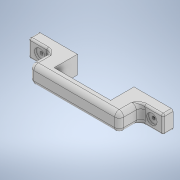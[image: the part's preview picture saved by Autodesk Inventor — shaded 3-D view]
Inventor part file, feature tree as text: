
AUTODESK INVENTOR PART (.ipt)
format: ipt  version: 2020 (Build 240168000, 168)  size: 222,208 bytes
history: native  units: mm
features: extrude x3, fillet x3, sketch x2, mirror x1, projected_geometry x1
ambient origin geometry x8: Origin, YZ Plane, XZ Plane, XY Plane, X Axis, Y Axis, Z Axis, Center Point
bodies: Solid1 (feature_tree)
feature tree (10):
  extrude  "Extrusion1"  Depth=50.0mm
  sketch  "Sketch2"  dims[d2=35.0mm d3=17.5mm d4=26.0mm d5=63.0mm d6=31.5mm d7=11.0mm d8=25.0mm d9=20.0mm d10=0.0mm d11=3.5mm d12=11.5mm d13=0.0mm d14=0.0mm d15=2.0mm d16=0.0mm d17=5.0mm d18=5.0mm d19=2.0mm]
  extrude  "Extrusion2"  Depth=2.0mm
  extrude  "Extrusion3"  Depth=2.0mm
  mirror  "Mirror1"
  fillet  "Fillet1"  Radius=63.0mm
  fillet  "Fillet2"  Radius=31.5mm
  fillet  "Fillet3"  Radius=11.0mm
  sketch  "Sketch1"  dims[d0=100.0mm d1=50.0mm]
  projected_geometry  "Projected Loop1"
